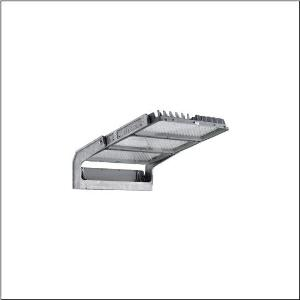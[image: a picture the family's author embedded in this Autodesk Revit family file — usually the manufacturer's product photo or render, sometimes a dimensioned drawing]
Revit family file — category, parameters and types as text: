
# Revit family: floodlight_fl_11_maxi_pro___rs07_5xa779128k01gb_3833
name_source: partatom
category: Lighting Fixtures
units: mm (PartAtom-declared; Revit-internal decimal feet)

## family parameters
Cut with Voids When Loaded = No
Host = Face
Light Source = No
Part Type = Normal
Room Calculation Point = No
Round Connector Dimension = Use Diameter
Shared = No

## types (1)
- --- (1 x LED, 149760 lm, 1285.1 W, 5700K)
    Apparent Load = 1285 VA
    CIE Flux Codes = 80 93 99 100 99
    Color Rendering = 80
    Color Temperature = 5700K
    Default Elevation = 1800 mm
    Description = Floodlight FL 11  maxi  pro floodlight; light control with lens of PMMA; cover panel of toughened safety glass, transparent; light distribution: RS07, rotationally symmetric direct distribution, LED; colour temperature: 5700K, rated luminous flux: 149.760lm, colour rendering: CRI > 80, light colour: 857; luminous efficacy: 117lm/W; brightness control: DALI 2; with terminal, 5-pole, max. 2.5mm², mains connection: 220..240V/380..400V AC, 50/60Hz, surge voltage resistance: line to ground: 10kV, LED service life up to 100,000h L90. Typical operating time: 1000h per year., ECG replaceable separately, LED unit replaceable without ESD environment, dustproof LED module, dimming range 10..100%; 1285W floodlight with 3x LED unit of diecast aluminium, coated grey; length: 1.003mm / width: 651mm / height: 338mm; mounting bracket, of diecast aluminium, uncoated, natural, equipment: Power, protection rating (complete): IP66; insulation class (complete): insulation class I (protective earthing); certification: CE, ENEC, VDE; ball protection: ball impact resistant, only for outdoor installations in the designated locations, permissible operating ambient temperature: -45..+55°C, permissible storage temperature: -40..+85°Cpackaging unit: 1 piece

Light Distribution: RS07
    Height = 320 mm
    Lamp = 1 x LED
    Lamp Light Flux = 149760 lm
    Lamp Power = 1285.1 W
    Lamp count = 1
    Length = 1002 mm
    Luminous efficacy = 117 lm/W
    Manufacturer = Siteco
    ModVariant = No
    Model = 5XA779128K01GB
    Mounting Place = Ceiling
    Mounting Type = Surface mounted
    Number of Poles = 1
    OnlyDefault = Yes
    Power Factor = 1
    Product Name = Floodlight FL 11 maxi pro | RS07
    Product group = floodlight | ceiling mounted
    ProductGroupID = 303
    Protection Class = Protection class I
    Protection Degree = IP 66
    RLX_Detail_Level = 1
    RLX_Emergency_Light_Flux = 0 lm
    RLX_Emergency_Type = 0
    RLX_Emergency_Type_DB = No
    RlxData = <blob elided: 40261 chars, md5=e5b6d1bb>
    Socket = socket
    Standby Power = 0 W
    System Light Flux = 149760 lm
    System Power = 1285 W
    Type Comments = factory setting: luminous flux: 100 % | dim-lin: 254 | 875 mA
    Type Image = l_1356210.jpg
    URL = http://relux.com
    VarID = @adj_039011
    Voltage = 0 V
    Weight = 0.00 kg
    Width = 655 mm

## geometry (parser evidence)
native form markers: Blend x4, Sweep x11
no freeform markers — native parametric forms only
